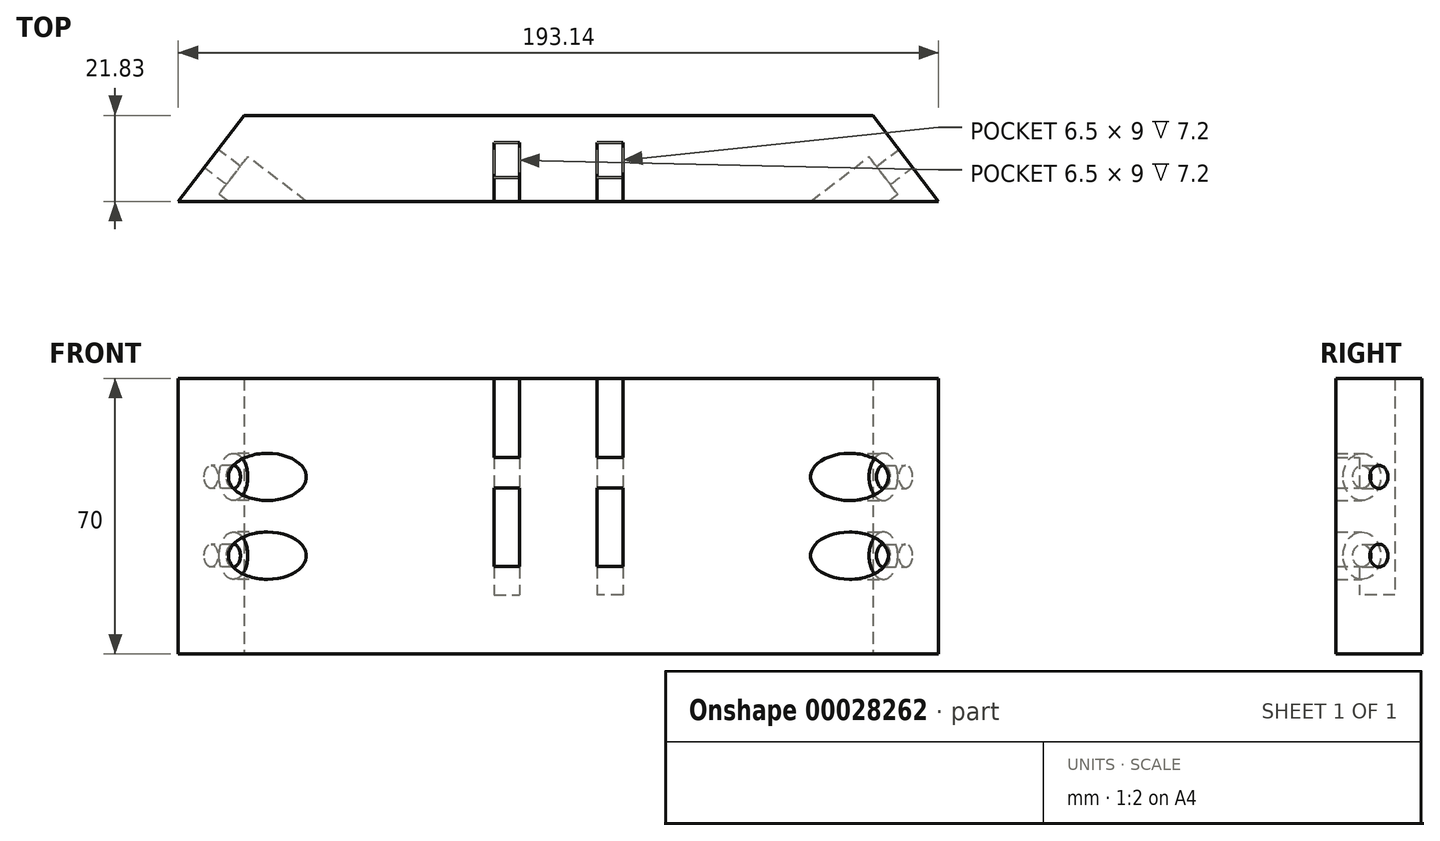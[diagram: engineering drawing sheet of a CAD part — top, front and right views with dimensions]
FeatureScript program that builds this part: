
annotation { "Feature Type Name" : "Feature", "Feature Type Description" : "" }
export const myFeature = defineFeature(function(context is Context, id is Id, definition is map)
    precondition{}
    {
        {
            var Q0;
            Q0=qCreatedBy(makeId("Top.planeOp"),FACE);
            var sketch = newSketch(context, id + "F0", { "sketchPlane" : qUnion([Q0]), "disableImprinting" : false});
            skLineSegment(sketch, "E0", {"start": v(-96.57, -6) * mm, "end": v(-79.89, 15.83) * mm});
            skLineSegment(sketch, "E1", {"start": v(-79.89, 15.83) * mm, "end": v(0, 15.83) * mm});
            skLineSegment(sketch, "E2", {"start": v(0, 0) * mm, "end": v(0, 49.64) * mm, "construction": true});
            skLineSegment(sketch, "E3", {"start": v(-96.57, -6) * mm, "end": v(0, -6) * mm});
            skLineSegment(sketch, "E4", {"start": v(-88.23, 4.92) * mm, "end": v(-36, -35) * mm, "construction": true});
            skLineSegment(sketch, "E5", {"start": v(0, 15.83) * mm, "end": v(0, -6) * mm});
            skSolve(sketch);
        }
        {
            var Q0;
            Q0 = qSketchRegion(id + "F0", true);
            extrude(context, id + "F1", {"entities" : qUnion([Q0]), "depth" : 70 * mm, "offsetDistance" : 25 * mm});
        }
        {
            var Q0;
            Q0=makeQuery(id+"F1.opExtrude","SWEPT_FACE",FACE,{"disambiguationData":[OSD([sQuery(id+"F0.wireOp",EDGE,"E0")])]});
            cPlane(context, id + "F2", {"entities" : qUnion([Q0]), "cplaneType" : CPlaneType.OFFSET, "offset" : 40 * mm, "oppositeDirection" : true, "width" : 150 * mm, "height" : 150 * mm});
        }
        {
            var Q0;
            Q0=qCreatedBy(id+"F2.planeOp",FACE);
            var sketch = newSketch(context, id + "F3", { "sketchPlane" : qUnion([Q0])});
            skCircle(sketch, "E6", {"center": v(49.67, 45) * mm, "radius": 2.9 * mm});
            skCircle(sketch, "E7", {"center": v(49.67, 25) * mm, "radius": 2.9 * mm});
            skLineSegment(sketch, "E8", {"start": v(49.67, 45) * mm, "end": v(49.67, 70) * mm, "construction": true});
            skLineSegment(sketch, "E9", {"start": v(49.67, 25) * mm, "end": v(49.67, 0) * mm, "construction": true});
            skSolve(sketch);
        }
        {
            var Q0;
            Q0=sQuery(id+"F3.wireOp",VERTEX,"E8.start");
            var Q1;
            Q1=sQuery(id+"F3.wireOp",VERTEX,"E7.center");
            var Q2;
            Q2=makeQuery(id+"F1.opExtrude","SWEPT_BODY",BODY,{"disambiguationData":[OSD([sQuery(id+"F0.wireOp",EDGE,"E0"),sQuery(id+"F0.wireOp",EDGE,"E1"),sQuery(id+"F0.wireOp",EDGE,"E3"),sQuery(id+"F0.wireOp",EDGE,"aecb69d0-cd61-4f2e-a3dc-bfc6b4541c090.MirrorCS"),sQuery(id+"F0.wireOp",EDGE,"aecb69d0-cd61-4f2e-a3dc-bfc6b4541c091.MirrorCS"),sQuery(id+"F0.wireOp",EDGE,"aecb69d0-cd61-4f2e-a3dc-bfc6b4541c092.MirrorCS")])]});
            hole(context, id + "F4", {"style" : HoleStyle.C_BORE, "endStyle" : HoleEndStyle.THROUGH, "oppositeDirection" : true, "holeDiameter" : 5.8 * mm, "cBoreDiameter" : 12 * mm, "cBoreDepth" : 3 * mm, "isTappedThrough" : true, "tappedDepth" : 12 * mm, "tapClearance" : 3, "locations" : qUnion([Q0, Q1]), "scope" : qUnion([Q2]), "startStyle" : HoleStartStyle.PART});
        }
        {
            var Q0;
            Q0=makeQuery(id+"F1.opExtrude","SWEPT_BODY",BODY,{"disambiguationData":[OSD([sQuery(id+"F0.wireOp",EDGE,"E0"),sQuery(id+"F0.wireOp",EDGE,"E1"),sQuery(id+"F0.wireOp",EDGE,"E3"),sQuery(id+"F0.wireOp",EDGE,"E5")])]});
            var Q1;
            Q1=qCreatedBy(makeId("Right.planeOp"),FACE);
            mirror(context, id + "F5", {"operationType" : NewBodyOperationType.ADD, "entities" : qUnion([Q0]), "mirrorPlane" : qUnion([Q1])});
        }
        {
            var Q0;
            Q0=qCreatedBy(makeId("Front.planeOp"),FACE);
            var sketch = newSketch(context, id + "F6", { "sketchPlane" : qUnion([Q0])});
            skLineSegment(sketch, "E10.bottom", {"start": v(-16.35, 42.2) * mm, "end": v(-9.85, 42.2) * mm});
            skLineSegment(sketch, "E10.top", {"start": v(-16.35, 22.2) * mm, "end": v(-9.85, 22.2) * mm});
            skLineSegment(sketch, "E10.left", {"start": v(-16.35, 42.2) * mm, "end": v(-16.35, 22.2) * mm});
            skLineSegment(sketch, "E10.right", {"start": v(-9.85, 42.2) * mm, "end": v(-9.85, 22.2) * mm});
            skLineSegment(sketch, "E11.0.1.0", {"start": v(-16.35, 70) * mm, "end": v(-16.35, 50) * mm});
            skLineSegment(sketch, "E11.0.1.1", {"start": v(-16.35, 50) * mm, "end": v(-9.85, 50) * mm});
            skLineSegment(sketch, "E11.0.1.2", {"start": v(-9.85, 70) * mm, "end": v(-9.85, 50) * mm});
            skLineSegment(sketch, "E11.0.1.3", {"start": v(-16.35, 70) * mm, "end": v(-9.85, 70) * mm});
            skLineSegment(sketch, "E11.1.0.0", {"start": v(9.85, 42.2) * mm, "end": v(9.85, 22.2) * mm});
            skLineSegment(sketch, "E11.1.0.1", {"start": v(9.85, 22.2) * mm, "end": v(16.35, 22.2) * mm});
            skLineSegment(sketch, "E11.1.0.2", {"start": v(16.35, 42.2) * mm, "end": v(16.35, 22.2) * mm});
            skLineSegment(sketch, "E11.1.0.3", {"start": v(9.85, 42.2) * mm, "end": v(16.35, 42.2) * mm});
            skLineSegment(sketch, "E11.1.1.0", {"start": v(9.85, 70) * mm, "end": v(9.85, 50) * mm});
            skLineSegment(sketch, "E11.1.1.1", {"start": v(9.85, 50) * mm, "end": v(16.35, 50) * mm});
            skLineSegment(sketch, "E11.1.1.2", {"start": v(16.35, 70) * mm, "end": v(16.35, 50) * mm});
            skLineSegment(sketch, "E11.1.1.3", {"start": v(9.85, 70) * mm, "end": v(16.35, 70) * mm});
            skLineSegment(sketch, "E11.direction1", {"start": v(-16.35, 22.2) * mm, "end": v(9.85, 22.2) * mm, "construction": true});
            skLineSegment(sketch, "E11.direction2", {"start": v(-16.35, 22.2) * mm, "end": v(-16.35, 50) * mm, "construction": true});
            skLineSegment(sketch, "E12", {"start": v(-9.85, 42.2) * mm, "end": v(9.85, 42.2) * mm, "construction": true});
            skLineSegment(sketch, "E13", {"start": v(0, 0) * mm, "end": v(0, 42.2) * mm, "construction": true});
            skSolve(sketch);
        }
        {
            var Q0;
            Q0 = qSketchRegion(id + "F6", true);
            extrude(context, id + "F7", {"entities" : qUnion([Q0]), "operationType" : NewBodyOperationType.REMOVE, "depth" : 25 * mm, "offsetDistance" : 25 * mm});
        }
        {
            var Q0;
            Q0=qCreatedBy(makeId("Front.planeOp"),FACE);
            var sketch = newSketch(context, id + "F8", { "sketchPlane" : qUnion([Q0])});
            skLineSegment(sketch, "E14.bottom", {"start": v(-16.35, 70) * mm, "end": v(-9.85, 70) * mm});
            skLineSegment(sketch, "E14.top", {"start": v(-16.35, 15) * mm, "end": v(-9.85, 15) * mm});
            skLineSegment(sketch, "E14.left", {"start": v(-16.35, 70) * mm, "end": v(-16.35, 15) * mm});
            skLineSegment(sketch, "E14.right", {"start": v(-9.85, 70) * mm, "end": v(-9.85, 15) * mm});
            skLineSegment(sketch, "E15.MirrorCS", {"start": v(16.35, 15) * mm, "end": v(9.85, 15) * mm});
            skLineSegment(sketch, "E16.MirrorCS", {"start": v(16.35, 70) * mm, "end": v(9.85, 70) * mm});
            skLineSegment(sketch, "E17.MirrorCS", {"start": v(16.35, 70) * mm, "end": v(16.35, 15) * mm});
            skLineSegment(sketch, "E18.MirrorCS", {"start": v(9.85, 70) * mm, "end": v(9.85, 15) * mm});
            skSolve(sketch);
        }
        {
            var Q0;
            Q0 = qSketchRegion(id + "F8", true);
            extrude(context, id + "F9", {"entities" : qUnion([Q0]), "operationType" : NewBodyOperationType.REMOVE, "oppositeDirection" : true, "depth" : 9 * mm, "offsetDistance" : 25 * mm});
        }
    });
